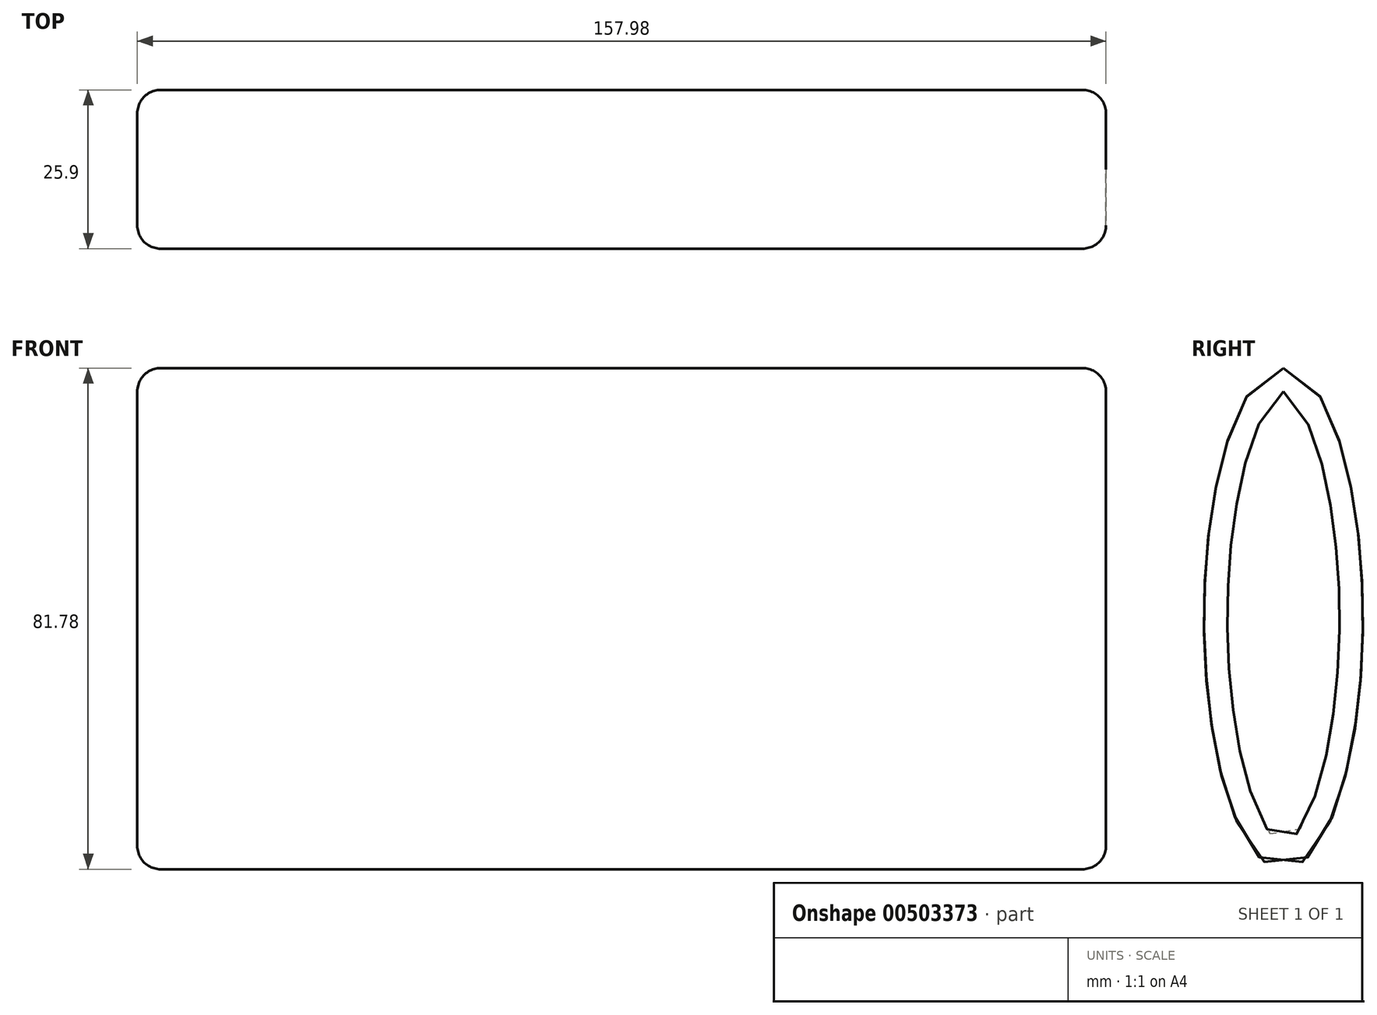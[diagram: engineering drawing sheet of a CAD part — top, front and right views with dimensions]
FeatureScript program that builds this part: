
annotation { "Feature Type Name" : "Feature", "Feature Type Description" : "" }
export const myFeature = defineFeature(function(context is Context, id is Id, definition is map)
    precondition{}
    {
        {
            var Q0;
            Q0=qCreatedBy(makeId("Right.planeOp"),FACE);
            var sketch = newSketch(context, id + "F0", { "sketchPlane" : qUnion([Q0])});
            skEllipse(sketch, "E0", {"center": v(0, 0) * mm, "majorRadius": 40.9 * mm, "minorRadius": 12.95 * mm, "majorAxis": v(0, 1)});
            skSolve(sketch);
        }
        {
            var Q0;
            Q0=makeQuery(id+"F0.imprint","IMPRINT",FACE,{"disambiguationData":[TD([[makeQuery(id+"F0.imprint","IMPRINT",EDGE,{"derivedFrom":sQuery(id+"F0.wireOp",EDGE,"E0")}),1.0]])]});
            extrude(context, id + "F1", {"entities" : qUnion([Q0]), "endBound" : BoundingType.SYMMETRIC, "depth" : 158 * mm});
        }
        {
            var Q0;
            Q0=makeQuery(id+"F1.opExtrude","CAP_EDGE",EDGE,{"disambiguationData":[OSD([sQuery(id+"F0.wireOp",EDGE,"E0")])],"isStart":false});
            var Q1;
            Q1=makeQuery(id+"F1.opExtrude","CAP_EDGE",EDGE,{"disambiguationData":[OSD([sQuery(id+"F0.wireOp",EDGE,"E0")])],"isStart":true});
            fillet(context, id + "F2", {"entities" : qUnion([Q0, Q1]), "radius" : 3.8 * mm, "tangentPropagation" : true, "allowEdgeOverflow" : false});
        }
    });
